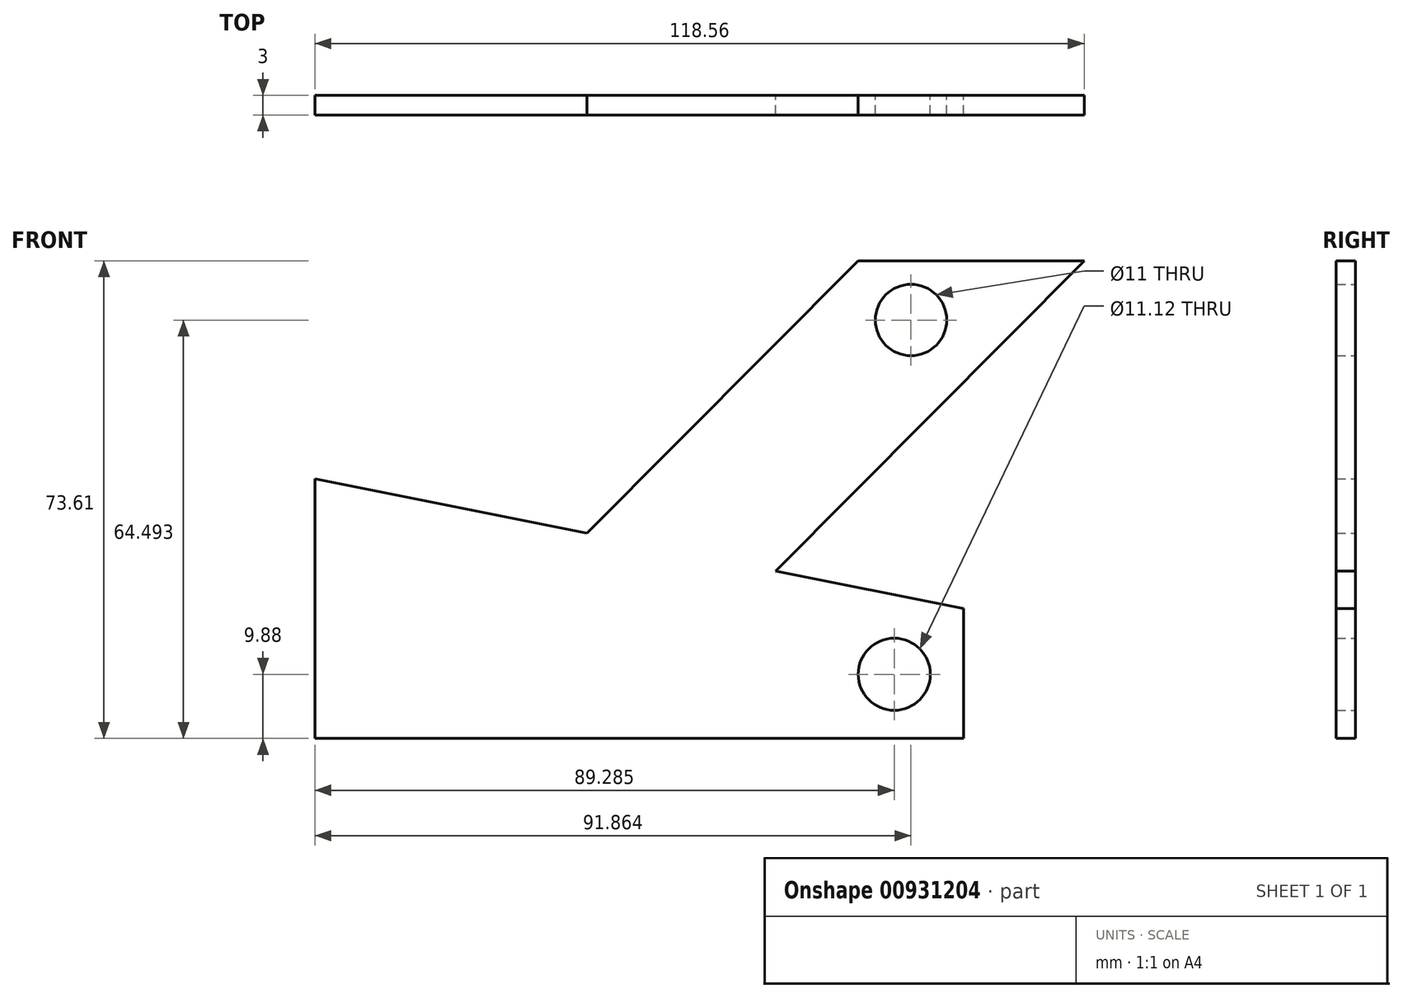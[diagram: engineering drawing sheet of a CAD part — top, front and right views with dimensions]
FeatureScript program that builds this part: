
annotation { "Feature Type Name" : "Feature", "Feature Type Description" : "" }
export const myFeature = defineFeature(function(context is Context, id is Id, definition is map)
    precondition{}
    {
        {
            var Q0;
            Q0=qCreatedBy(makeId("Front.planeOp"),FACE);
            var sketch = newSketch(context, id + "F0", { "sketchPlane" : qUnion([Q0])});
            skLineSegment(sketch, "E0", {"start": v(-100, 0) * mm, "end": v(0, 0) * mm});
            skLineSegment(sketch, "E1", {"start": v(0, 0) * mm, "end": v(0, 20) * mm});
            skLineSegment(sketch, "E2", {"start": v(-100, 0) * mm, "end": v(-100, 40) * mm});
            skLineSegment(sketch, "E3", {"start": v(-100, 40) * mm, "end": v(0, 20) * mm});
            skCircle(sketch, "E4", {"center": v(-10.71, 9.88) * mm, "radius": 5.56 * mm});
            skLineSegment(sketch, "E5", {"start": v(-58.04, 31.6) * mm, "end": v(-16.28, 73.6) * mm});
            skLineSegment(sketch, "E6", {"start": v(-28.99, 25.8) * mm, "end": v(18.56, 73.6) * mm});
            skLineSegment(sketch, "E7", {"start": v(18.56, 73.6) * mm, "end": v(-16.28, 73.6) * mm});
            skCircle(sketch, "E8", {"center": v(-8.14, 64.5) * mm, "radius": 5.5 * mm});
            skSolve(sketch);
        }
        {
            var Q0;
            {var subQ1=sQuery(id+"F0.wireOp",EDGE,"E5");Q0=makeQuery(id+"F0.imprint","IMPRINT",FACE,{"disambiguationData":[TD([[makeQuery(id+"F0.imprint","IMPRINT",EDGE,{"derivedFrom":subQ1}),-1.0]])]});}
            var Q1;
            Q1=makeQuery(id+"F0.imprint","IMPRINT",FACE,{"disambiguationData":[TD([[makeQuery(id+"F0.imprint","IMPRINT",EDGE,{"derivedFrom":sQuery(id+"F0.wireOp",EDGE,"E0")}),1.0]])]});
            extrude(context, id + "F1", {"entities" : qUnion([Q0, Q1]), "depth" : 3 * mm, "offsetDistance" : 25 * mm});
        }
    });
